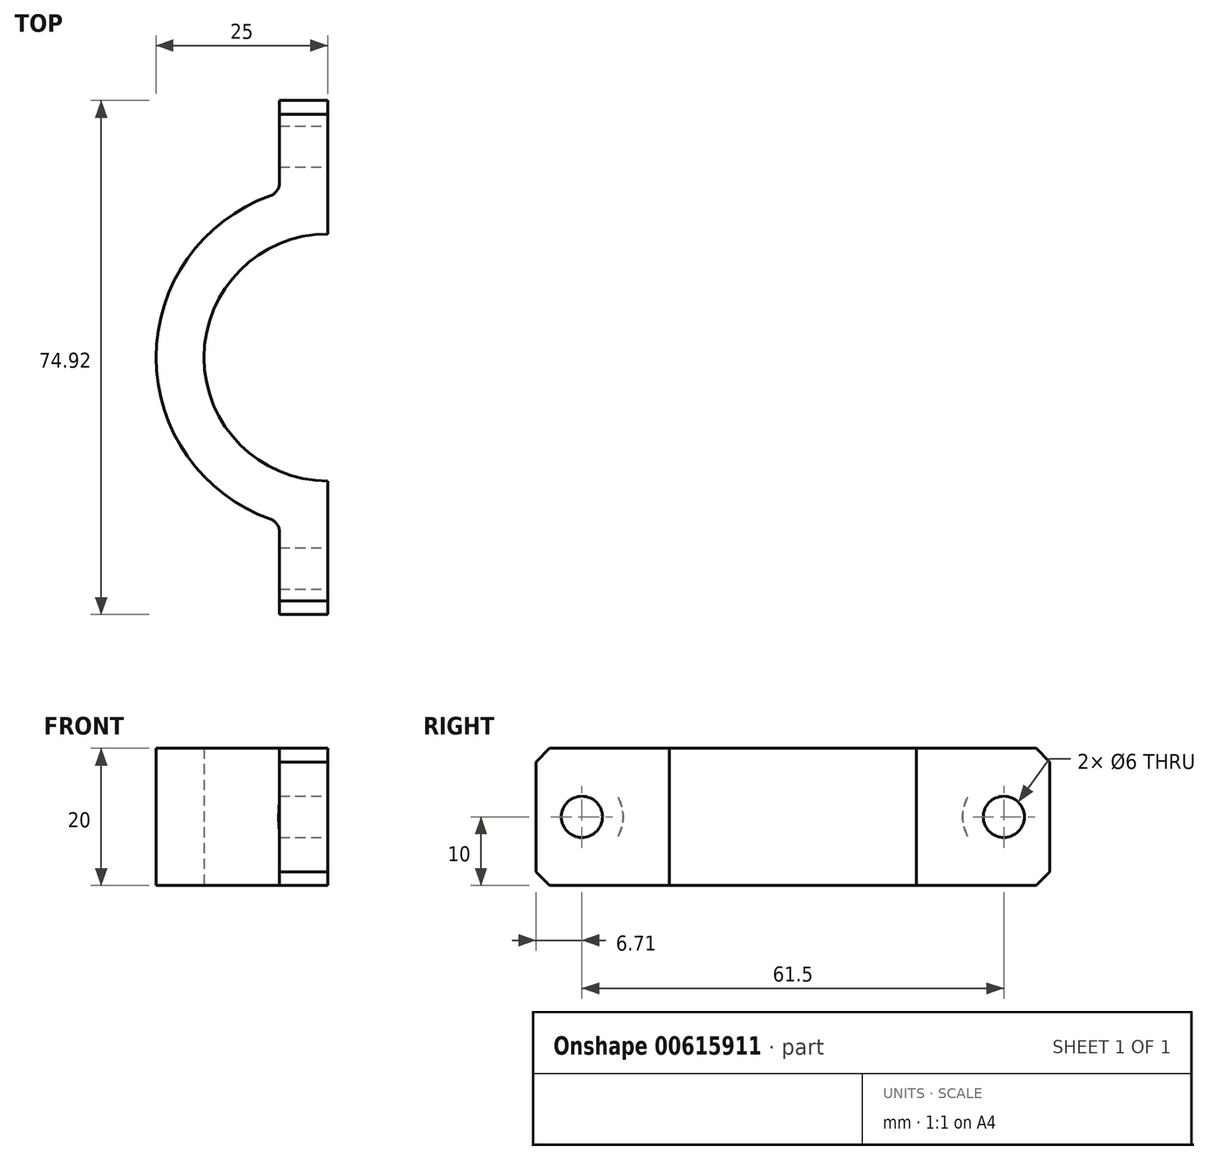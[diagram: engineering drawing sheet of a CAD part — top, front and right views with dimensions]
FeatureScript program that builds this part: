
annotation { "Feature Type Name" : "Feature", "Feature Type Description" : "" }
export const myFeature = defineFeature(function(context is Context, id is Id, definition is map)
    precondition{}
    {
        {
            var Q0;
            Q0=qCreatedBy(makeId("Top.planeOp"),FACE);
            var sketch = newSketch(context, id + "F0", { "sketchPlane" : qUnion([Q0])});
            skLineSegment(sketch, "E0", {"start": v(0, 22.5) * mm, "end": v(0, 37.46) * mm});
            skLineSegment(sketch, "E1", {"start": v(0, 37.46) * mm, "end": v(-7, 37.46) * mm});
            skLineSegment(sketch, "E2.MirrorCS", {"start": v(0, -22.5) * mm, "end": v(0, -37.46) * mm});
            skLineSegment(sketch, "E3.MirrorCS", {"start": v(0, -37.46) * mm, "end": v(-7, -37.46) * mm});
            skLineSegment(sketch, "E4", {"start": v(0, -22.5) * mm, "end": v(0, -18) * mm});
            skLineSegment(sketch, "E5", {"start": v(0, 22.5) * mm, "end": v(0, 18) * mm});
            skArc(sketch, "E6", {"start": v(0, -18) * mm, "mid": v(-18, 0) * mm, "end": v(0, 18) * mm});
            skArc(sketch, "E7", {"start": v(-7, 24) * mm, "mid": v(-25, 0) * mm, "end": v(-7, -24) * mm});
            skLineSegment(sketch, "E8", {"start": v(-7, -37.46) * mm, "end": v(-7, -24) * mm});
            skLineSegment(sketch, "E9", {"start": v(-7, 37.46) * mm, "end": v(-7, 24) * mm});
            skSolve(sketch);
        }
        {
            var Q0;
            Q0 = qSketchRegion(id + "F0", true);
            extrude(context, id + "F1", {"entities" : qUnion([Q0]), "depth" : 20 * mm, "offsetDistance" : 25 * mm});
        }
        {
            var Q0;
            Q0=qCreatedBy(makeId("Right.planeOp"),FACE);
            var sketch = newSketch(context, id + "F2", { "sketchPlane" : qUnion([Q0])});
            skPoint(sketch, "E10", {"position": v(-30.75, 10) * mm});
            skPoint(sketch, "E11", {"position": v(30.75, 10) * mm});
            skSolve(sketch);
        }
        {
            var Q0;
            Q0=sQuery(id+"F2.wireOp",VERTEX,"7d2de1e9-4c74-4a9e-87fa-11e6430826c8");
            var Q1;
            Q1=sQuery(id+"F2.wireOp",VERTEX,"70abb4a4-c087-47f1-a3d9-a49e52b7706c");
            var Q2;
            Q2=sQuery(id+"F2.wireOp",VERTEX,"E10");
            var Q3;
            Q3=sQuery(id+"F2.wireOp",VERTEX,"E11");
            var Q4;
            Q4=makeQuery(id+"F1.opExtrude","SWEPT_BODY",BODY,{"disambiguationData":[OSD([sQuery(id+"F0.wireOp",EDGE,"E0"),sQuery(id+"F0.wireOp",EDGE,"E1"),sQuery(id+"F0.wireOp",EDGE,"2xBRe8jf-aJMX-0015-EjRJ-wM6UxoX7mEIy"),sQuery(id+"F0.wireOp",EDGE,"E2.MirrorCS"),sQuery(id+"F0.wireOp",EDGE,"bf2c515f-6c96-4f71-ba25-24dc51d3ef061.MirrorCS"),sQuery(id+"F0.wireOp",EDGE,"E3.MirrorCS"),sQuery(id+"F0.wireOp",EDGE,"naDVgpl3-CwDr-0Aqk-OrPx-2DM68l7VPjmR"),sQuery(id+"F0.wireOp",EDGE,"IEYaewgz-XrwC-X3By-oALP-7GhbgWkhWOZ3"),sQuery(id+"F0.wireOp",EDGE,"P1K1naN9-KfKw-z1ZP-l3DC-rS5adNtSIpyA"),sQuery(id+"F0.wireOp",EDGE,"Si4qHKFM-QbOo-PcNs-thFO-ZrQPA1XW8fQx")])]});
            hole(context, id + "F3", {"style" : HoleStyle.SIMPLE, "endStyle" : HoleEndStyle.THROUGH, "holeDiameter" : 6 * mm, "majorDiameter" : 5 * mm, "isTappedThrough" : true, "tappedDepth" : 12 * mm, "tapClearance" : 3, "locations" : qUnion([Q0, Q1, Q2, Q3]), "scope" : qUnion([Q4])});
        }
        {
            var Q0;
            Q0=makeQuery(id+"F1.opExtrude","CAP_EDGE",EDGE,{"disambiguationData":[OSD([sQuery(id+"F0.wireOp",EDGE,"E3.MirrorCS")])],"isStart":false});
            var Q1;
            Q1=makeQuery(id+"F1.opExtrude","CAP_EDGE",EDGE,{"disambiguationData":[OSD([sQuery(id+"F0.wireOp",EDGE,"E3.MirrorCS")])],"isStart":true});
            var Q2;
            Q2=makeQuery(id+"F1.opExtrude","CAP_EDGE",EDGE,{"disambiguationData":[OSD([sQuery(id+"F0.wireOp",EDGE,"E1")])],"isStart":false});
            var Q3;
            Q3=makeQuery(id+"F1.opExtrude","CAP_EDGE",EDGE,{"disambiguationData":[OSD([sQuery(id+"F0.wireOp",EDGE,"E1")])],"isStart":true});
            chamfer(context, id + "F4", {"entities" : qUnion([Q0, Q1, Q2, Q3]), "width" : 2 * mm, "tangentPropagation" : true});
        }
        {
            var Q0;
            Q0=makeQuery(id+"F1.opExtrude","SWEPT_EDGE",EDGE,{"disambiguationData":[OSD([sQuery(id+"F0.wireOp",EDGE,"E7"),sQuery(id+"F0.wireOp",EDGE,"E8")])]});
            var Q1;
            Q1=makeQuery(id+"F1.opExtrude","SWEPT_EDGE",EDGE,{"disambiguationData":[OSD([sQuery(id+"F0.wireOp",EDGE,"E7"),sQuery(id+"F0.wireOp",EDGE,"E9")])]});
            fillet(context, id + "F5", {"entities" : qUnion([Q0, Q1]), "tangentPropagation" : true, "radius" : 2 * mm, "defaultsChanged" : true, "vertexSettings" : [], "allowEdgeOverflow" : false});
        }
        {
            var Q0;
            Q0=makeQuery(id+"F1.opExtrude","SWEPT_FACE",FACE,{"disambiguationData":[OSD([sQuery(id+"F0.wireOp",EDGE,"E8")])]});
            var sketch = newSketch(context, id + "F6", { "sketchPlane" : qUnion([Q0])});
            skCircle(sketch, "E12", {"center": v(30.75, 10) * mm, "radius": 6 * mm});
            skSolve(sketch);
        }
        {
            var Q0;
            Q0=sQuery(id+"F6.wireOp",VERTEX,"E12.center");
            var Q1;
            Q1=makeQuery(id+"F1.opExtrude","SWEPT_BODY",BODY,{"disambiguationData":[OSD([sQuery(id+"F0.wireOp",EDGE,"E0"),sQuery(id+"F0.wireOp",EDGE,"E1"),sQuery(id+"F0.wireOp",EDGE,"E2.MirrorCS"),sQuery(id+"F0.wireOp",EDGE,"E3.MirrorCS"),sQuery(id+"F0.wireOp",EDGE,"E4"),sQuery(id+"F0.wireOp",EDGE,"E5"),sQuery(id+"F0.wireOp",EDGE,"E6"),sQuery(id+"F0.wireOp",EDGE,"E7"),sQuery(id+"F0.wireOp",EDGE,"E8"),sQuery(id+"F0.wireOp",EDGE,"E9")])]});
            hole(context, id + "F7", {"style" : HoleStyle.SIMPLE, "endStyle" : HoleEndStyle.BLIND, "oppositeDirection" : true, "holeDiameter" : 12 * mm, "majorDiameter" : 5 * mm, "holeDepth" : 12 * mm, "isTappedThrough" : true, "tappedDepth" : 12 * mm, "tapClearance" : 3, "locations" : qUnion([Q0]), "scope" : qUnion([Q1])});
        }
        {
            var Q0;
            Q0=makeQuery(id+"F1.opExtrude","SWEPT_FACE",FACE,{"disambiguationData":[OSD([sQuery(id+"F0.wireOp",EDGE,"E9")])]});
            var sketch = newSketch(context, id + "F8", { "sketchPlane" : qUnion([Q0])});
            skCircle(sketch, "E13", {"center": v(-30.75, 10) * mm, "radius": 6 * mm});
            skSolve(sketch);
        }
        {
            var Q0;
            Q0=sQuery(id+"F8.wireOp",VERTEX,"E13.center");
            var Q1;
            Q1=makeQuery(id+"F1.opExtrude","SWEPT_BODY",BODY,{"disambiguationData":[OSD([sQuery(id+"F0.wireOp",EDGE,"E0"),sQuery(id+"F0.wireOp",EDGE,"E1"),sQuery(id+"F0.wireOp",EDGE,"E2.MirrorCS"),sQuery(id+"F0.wireOp",EDGE,"E3.MirrorCS"),sQuery(id+"F0.wireOp",EDGE,"E4"),sQuery(id+"F0.wireOp",EDGE,"E5"),sQuery(id+"F0.wireOp",EDGE,"E6"),sQuery(id+"F0.wireOp",EDGE,"E7"),sQuery(id+"F0.wireOp",EDGE,"E8"),sQuery(id+"F0.wireOp",EDGE,"E9")])]});
            hole(context, id + "F9", {"style" : HoleStyle.SIMPLE, "endStyle" : HoleEndStyle.BLIND, "oppositeDirection" : true, "holeDiameter" : 12 * mm, "majorDiameter" : 5 * mm, "holeDepth" : 12 * mm, "isTappedThrough" : true, "tappedDepth" : 12 * mm, "tapClearance" : 3, "locations" : qUnion([Q0]), "scope" : qUnion([Q1])});
        }
    });
